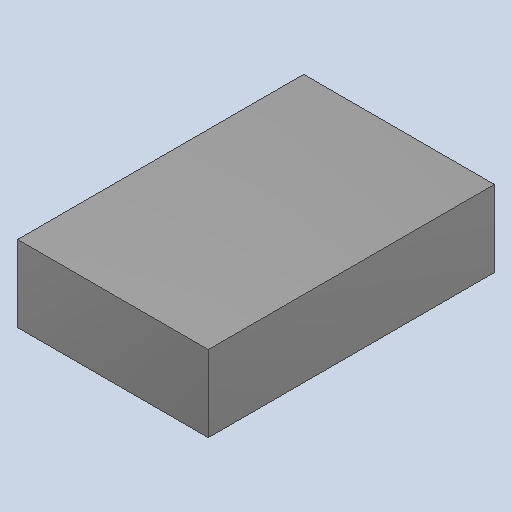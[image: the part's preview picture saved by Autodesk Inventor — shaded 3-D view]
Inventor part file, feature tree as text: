
AUTODESK INVENTOR PART (.ipt)
format: ipt  version: 2022.1 (Build 261234000, 234)  size: 85,504 bytes
history: imported  units: mm
features: imported_body x1
ambient origin geometry x8: Origin, YZ Plane, XZ Plane, XY Plane, X Axis, Y Axis, Z Axis, Center Point
bodies: Solid1 (imported_parasolid)
feature tree (1):
  imported_body  NMx_Import_Brep_tag  [imported B-rep: ~6 faces, bbox_mm=[2.0, 0.8, 3.0]]
